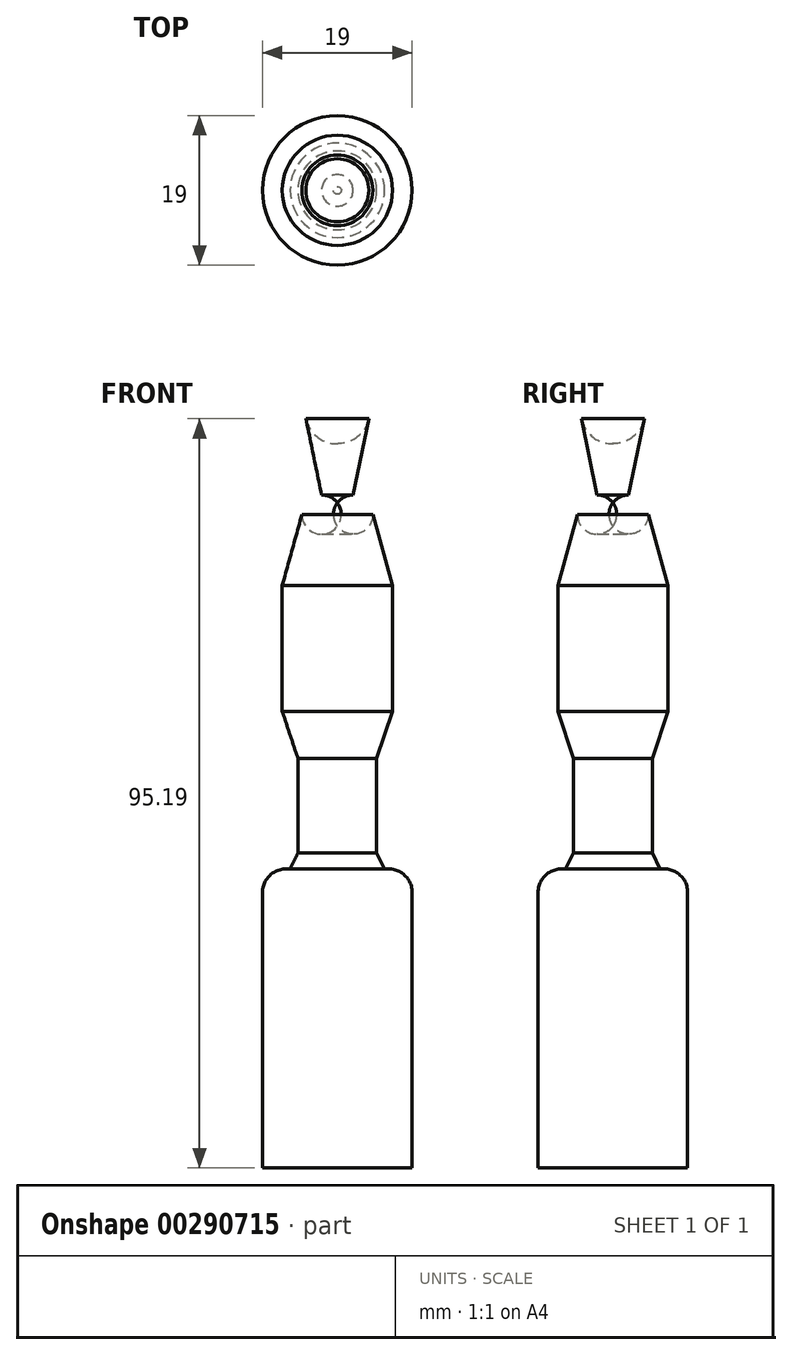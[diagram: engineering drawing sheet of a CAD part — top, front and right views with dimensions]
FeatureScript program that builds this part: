
annotation { "Feature Type Name" : "Feature", "Feature Type Description" : "" }
export const myFeature = defineFeature(function(context is Context, id is Id, definition is map)
    precondition{}
    {
        {
            var Q0;
            Q0=qCreatedBy(makeId("Front.planeOp"),FACE);
            var sketch = newSketch(context, id + "F0", { "sketchPlane" : qUnion([Q0])});
            skArc(sketch, "E0", {"start": v(4, -4.8) * mm, "mid": v(3.16, -1.44) * mm, "end": v(0, 0) * mm});
            skLineSegment(sketch, "E1", {"start": v(4, -4.8) * mm, "end": v(2, -14.5) * mm});
            skArc(sketch, "E2", {"start": v(4.5, -17) * mm, "mid": v(3.77, -15.23) * mm, "end": v(2, -14.5) * mm});
            skLineSegment(sketch, "E3", {"start": v(4.5, -17) * mm, "end": v(7, -26) * mm});
            skLineSegment(sketch, "E4", {"start": v(7, -26) * mm, "end": v(7, -42) * mm});
            skLineSegment(sketch, "E5", {"start": v(7, -42) * mm, "end": v(5, -48) * mm});
            skLineSegment(sketch, "E6", {"start": v(5, -48) * mm, "end": v(5, -60) * mm});
            skLineSegment(sketch, "E7", {"start": v(5, -60) * mm, "end": v(6, -62) * mm});
            skLineSegment(sketch, "E8", {"start": v(6, -62) * mm, "end": v(6.5, -62) * mm});
            skArc(sketch, "E9", {"start": v(9.5, -65) * mm, "mid": v(8.62, -62.88) * mm, "end": v(6.5, -62) * mm});
            skLineSegment(sketch, "E10", {"start": v(9.5, -65) * mm, "end": v(9.5, -100) * mm});
            skLineSegment(sketch, "E11", {"start": v(9.5, -100) * mm, "end": v(0, -100) * mm});
            skLineSegment(sketch, "E12", {"start": v(0, -100) * mm, "end": v(0, 0) * mm});
            skSolve(sketch);
        }
        {
            var Q0;
            Q0=makeQuery(id+"F0.imprint","IMPRINT",FACE,{"disambiguationData":[TD([[makeQuery(id+"F0.imprint","IMPRINT",EDGE,{"derivedFrom":sQuery(id+"F0.wireOp",EDGE,"E0")}),1.0]])]});
            var Q1;
            Q1=sQuery(id+"F0.wireOp",EDGE,"E12");
            revolve(context, id + "F1", {"entities" : qUnion([Q0]), "axis" : qUnion([Q1]), "revolveType" : RevolveType.FULL});
        }
    });
